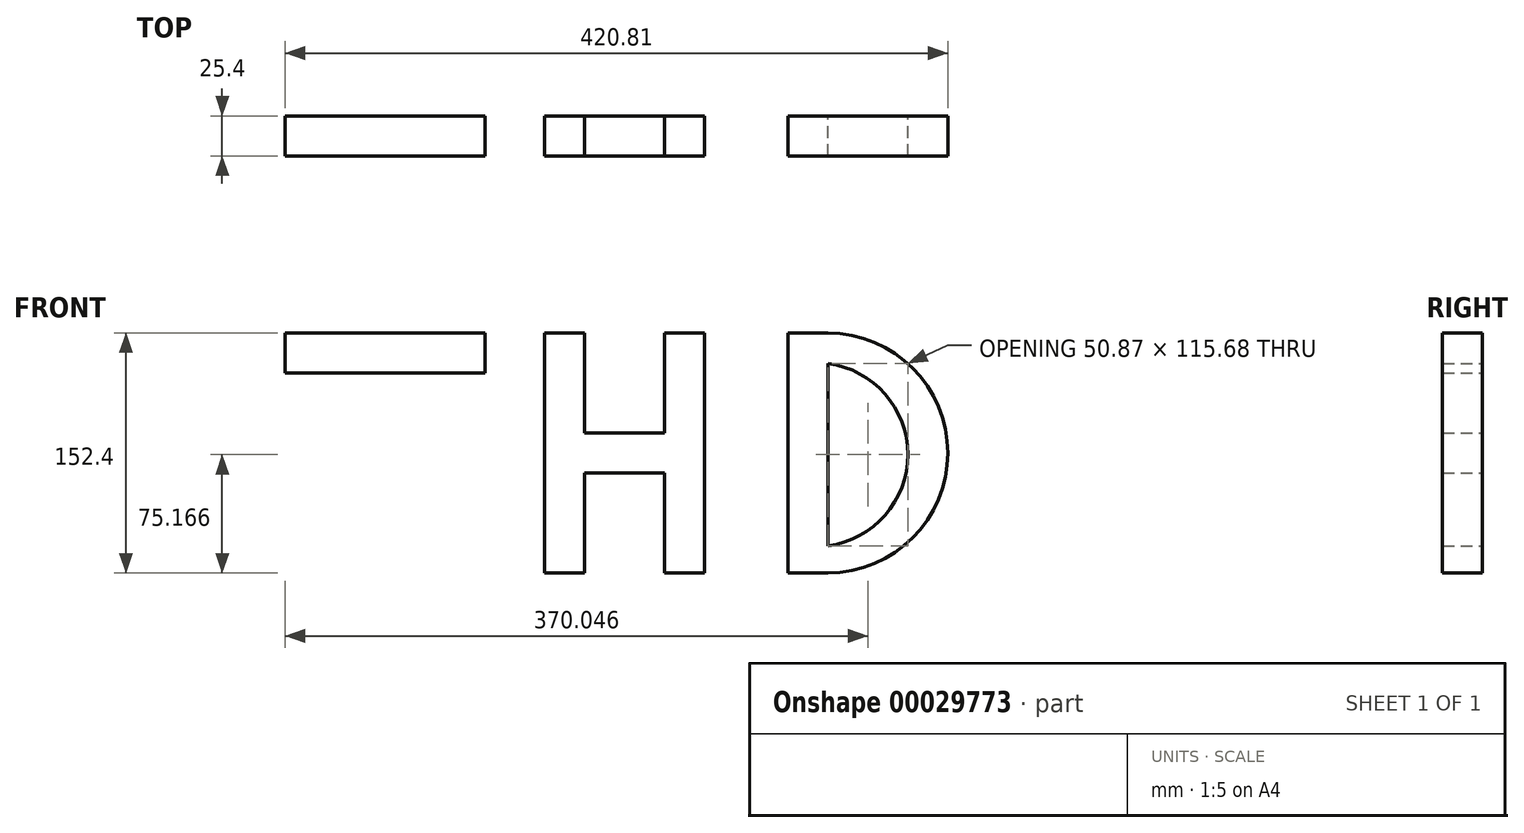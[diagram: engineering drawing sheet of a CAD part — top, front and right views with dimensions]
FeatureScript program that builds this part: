
annotation { "Feature Type Name" : "Feature", "Feature Type Description" : "" }
export const myFeature = defineFeature(function(context is Context, id is Id, definition is map)
    precondition{}
    {
        {
            var Q0;
            Q0=qCreatedBy(makeId("Front.planeOp"),FACE);
            var sketch = newSketch(context, id + "F0", { "sketchPlane" : qUnion([Q0])});
            skLineSegment(sketch, "E0.bottom", {"start": v(-215.43, 82.55) * mm, "end": v(-88.43, 82.55) * mm});
            skLineSegment(sketch, "E0.top", {"start": v(-215.43, 57.15) * mm, "end": v(-88.43, 57.15) * mm});
            skLineSegment(sketch, "E0.left", {"start": v(-215.43, 82.55) * mm, "end": v(-215.43, 57.15) * mm});
            skLineSegment(sketch, "E0.right", {"start": v(-88.43, 82.55) * mm, "end": v(-88.43, 57.15) * mm});
            skLineSegment(sketch, "E1.bottom", {"start": v(-164.63, 57.15) * mm, "end": v(-139.23, 57.15) * mm});
            skLineSegment(sketch, "E1.top", {"start": v(-164.63, -69.85) * mm, "end": v(-139.23, -69.85) * mm});
            skLineSegment(sketch, "E1.left", {"start": v(-164.63, 57.15) * mm, "end": v(-164.63, -69.85) * mm});
            skLineSegment(sketch, "E1.right", {"start": v(-139.23, 57.15) * mm, "end": v(-139.23, -69.85) * mm});
            skLineSegment(sketch, "E2", {"start": v(-164.63, -69.85) * mm, "end": v(250.43, -69.85) * mm, "construction": true});
            skLineSegment(sketch, "E3.bottom", {"start": v(-50.82, -69.85) * mm, "end": v(-25.42, -69.85) * mm});
            skLineSegment(sketch, "E3.top", {"start": v(-50.82, 82.55) * mm, "end": v(-25.42, 82.55) * mm});
            skLineSegment(sketch, "E3.left", {"start": v(-50.82, -69.85) * mm, "end": v(-50.82, 82.55) * mm});
            skLineSegment(sketch, "E3.right", {"start": v(-25.42, -69.85) * mm, "end": v(-25.42, 82.55) * mm});
            skLineSegment(sketch, "E4.bottom", {"start": v(50.78, -69.85) * mm, "end": v(25.38, -69.85) * mm});
            skLineSegment(sketch, "E4.top", {"start": v(50.78, 82.55) * mm, "end": v(25.38, 82.55) * mm});
            skLineSegment(sketch, "E4.left", {"start": v(50.78, -69.85) * mm, "end": v(50.78, 82.55) * mm});
            skLineSegment(sketch, "E4.right", {"start": v(25.38, -69.85) * mm, "end": v(25.38, 82.55) * mm});
            skLineSegment(sketch, "E5.bottom", {"start": v(-25.42, 19.05) * mm, "end": v(25.38, 19.05) * mm});
            skLineSegment(sketch, "E5.top", {"start": v(-25.42, -6.35) * mm, "end": v(25.38, -6.35) * mm});
            skLineSegment(sketch, "E5.left", {"start": v(-25.42, 19.05) * mm, "end": v(-25.42, -6.35) * mm});
            skLineSegment(sketch, "E5.right", {"start": v(25.38, 19.05) * mm, "end": v(25.38, -6.35) * mm});
            skLineSegment(sketch, "E6.bottom", {"start": v(103.78, -69.85) * mm, "end": v(129.18, -69.85) * mm});
            skLineSegment(sketch, "E6.top", {"start": v(103.78, 82.55) * mm, "end": v(129.18, 82.55) * mm});
            skLineSegment(sketch, "E6.left", {"start": v(103.78, -69.85) * mm, "end": v(103.78, 82.55) * mm});
            skLineSegment(sketch, "E6.right", {"start": v(129.18, -69.85) * mm, "end": v(129.18, 82.55) * mm});
            skArc(sketch, "E7", {"start": v(129.18, -69.85) * mm, "mid": v(205.38, 6.35) * mm, "end": v(129.18, 82.55) * mm});
            skArc(sketch, "E8", {"start": v(129.18, -52.52) * mm, "mid": v(180.05, 5.32) * mm, "end": v(129.18, 63.15) * mm});
            skSolve(sketch);
        }
        {
            var Q0;
            Q0=makeQuery(id+"F0.imprint","IMPRINT",FACE,{"disambiguationData":[TD([[makeQuery(id+"F0.imprint","IMPRINT",EDGE,{"derivedFrom":sQuery(id+"F0.wireOp",EDGE,"E0.bottom")}),-1.0]])]});
            var Q1;
            Q1=makeQuery(id+"F0.imprint","IMPRINT",FACE,{"disambiguationData":[TD([[makeQuery(id+"F0.imprint","IMPRINT",EDGE,{"derivedFrom":sQuery(id+"F0.wireOp",EDGE,"E1.bottom")}),-1.0]])]});
            var Q2;
            {var subQ3=sQuery(id+"F0.wireOp",EDGE,"E3.bottom");Q2=makeQuery(id+"F0.imprint","IMPRINT",FACE,{"disambiguationData":[TD([[makeQuery(id+"F0.imprint","IMPRINT",EDGE,{"derivedFrom":subQ3}),1.0]])]});}
            var Q3;
            Q3=makeQuery(id+"F0.imprint","IMPRINT",FACE,{"disambiguationData":[TD([[makeQuery(id+"F0.imprint","IMPRINT",EDGE,{"derivedFrom":sQuery(id+"F0.wireOp",EDGE,"E5.bottom")}),-1.0]])]});
            var Q4;
            {var subQ3=sQuery(id+"F0.wireOp",EDGE,"E4.bottom");Q4=makeQuery(id+"F0.imprint","IMPRINT",FACE,{"disambiguationData":[TD([[makeQuery(id+"F0.imprint","IMPRINT",EDGE,{"derivedFrom":subQ3}),-1.0]])]});}
            var Q5;
            {var subQ6=sQuery(id+"F0.wireOp",EDGE,"E6.bottom");Q5=makeQuery(id+"F0.imprint","IMPRINT",FACE,{"disambiguationData":[TD([[makeQuery(id+"F0.imprint","IMPRINT",EDGE,{"derivedFrom":subQ6}),1.0]])]});}
            var Q6;
            {var subQ1=sQuery(id+"F0.wireOp",EDGE,"E7");Q6=makeQuery(id+"F0.imprint","IMPRINT",FACE,{"disambiguationData":[TD([[makeQuery(id+"F0.imprint","IMPRINT",EDGE,{"derivedFrom":subQ1}),1.0]])]});}
            extrude(context, id + "F1", {"entities" : qUnion([Q0, Q1, Q2, Q3, Q4, Q5, Q6]), "depth" : 25.4 * mm});
        }
    });
